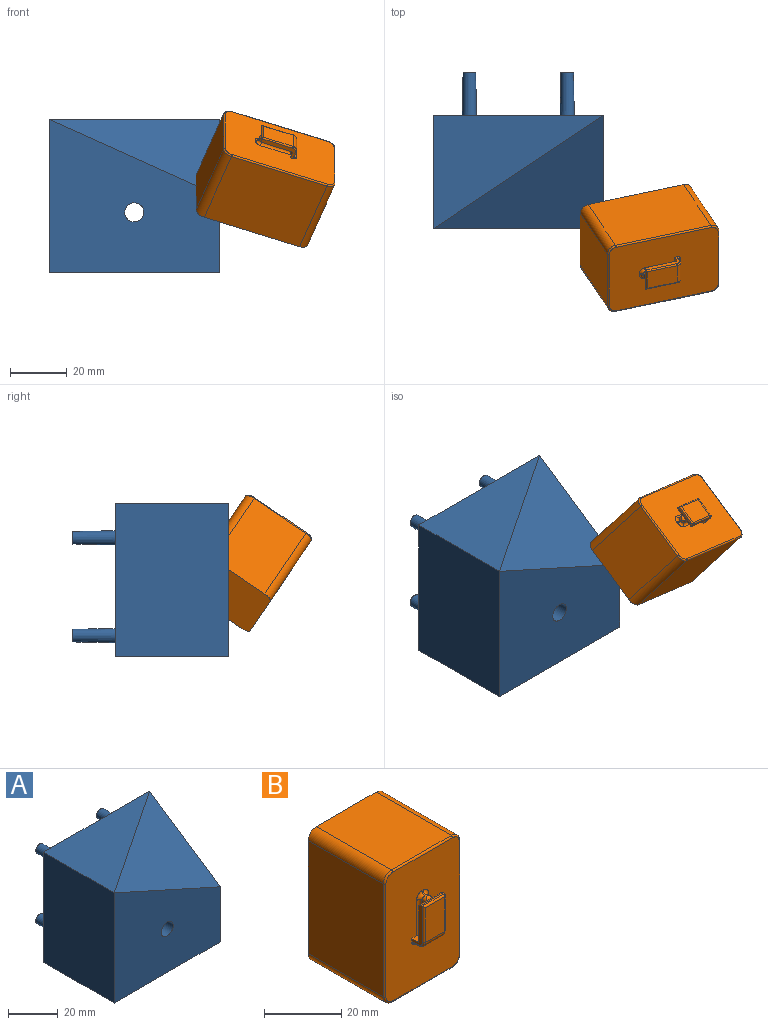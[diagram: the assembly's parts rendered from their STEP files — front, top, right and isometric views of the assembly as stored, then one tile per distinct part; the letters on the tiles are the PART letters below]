
ASSEMBLY  parts=2 mates=1
PART A: 16 faces, bbox 60x55x54 mm
  f0: plane 54x40mm, normal (1,0,0), area 1620mm2, adj f2,f4,f5,f15
  f1: plane 60x40mm, normal (0,0,1), area 1200mm2, adj f3,f5,f15
  f2: plane 60x54mm, normal (0,-1,0), area 2394.2mm2, adj f0,f3,f4,f14,f15
  f3: plane 54x40mm, normal (-1,0,0), area 2160mm2, adj f1,f2,f4,f5
  f4: plane 60x40mm, normal (0,0,-1), area 2400mm2, adj f0,f2,f3,f5
  f5: plane 60x54mm, normal (0,1,0), area 3125.7mm2, adj f0,f1,f3,f4,f6,f8,f10,f12
  f6: cone r=2.5mm half-angle=1deg, axis (0,-1,0), area 223.3mm2, adj f5,f7
  f7: plane 4.48x4.48mm, normal (0,1,0), area 15.7mm2, adj f6
  f8: cone r=2.5mm half-angle=1deg, axis (0,-1,0), area 223.3mm2, adj f5,f9
  f9: plane 4.48x4.48mm, normal (0,1,0), area 15.7mm2, adj f8
  f10: cone r=2.5mm half-angle=1deg, axis (0,-1,0), area 223.3mm2, adj f5,f11
  f11: plane 4.48x4.48mm, normal (0,1,0), area 15.7mm2, adj f10
  f12: cone r=2.5mm half-angle=1deg, axis (0,-1,0), area 223.3mm2, adj f5,f13
  f13: plane 4.48x4.48mm, normal (0,1,0), area 15.7mm2, adj f12
  f14: cylinder r=3.38mm len=40mm, axis (0,-1,0), area 848.2mm2, adj f2,f5
  f15: plane 60x40mm, normal (0.35,-0.52,0.78), area 1545.2mm2, adj f0,f1,f2
PART B: 49 faces, bbox 28.5x32.8x42.4 mm
  f0: plane 35.8x27.5mm, normal (1,0,0), area 984.5mm2, adj f1,f7,f46,f48
  f1: cylinder r=3mm len=27.5mm, axis (0,1,0), area 129.6mm2, adj f0,f2,f44,f48
  f2: plane 27.5x21.9mm, normal (0,0,1), area 602.2mm2, adj f1,f3,f42,f48
  f3: cylinder r=3mm len=27.5mm, axis (0,1,0), area 129.6mm2, adj f2,f4,f40,f48
  f4: plane 35.8x27.5mm, normal (-1,0,0), area 984.5mm2, adj f3,f5,f41,f48
  f5: cylinder r=3mm len=27.5mm, axis (0,1,0), area 129.6mm2, adj f4,f6,f43,f48
  f6: plane 27.5x21.9mm, normal (0,0,-1), area 602.2mm2, adj f5,f7,f45,f48
  f7: cylinder r=3mm len=27.5mm, axis (0,1,0), area 129.6mm2, adj f0,f6,f47,f48
  f8: plane 40.95x27.05mm, normal (0,-1,0), area 1016.5mm2, adj f9,f11,f12,f16,f18,f20,f22,f23
  f9: plane 13.42x4mm, normal (-1,0,0), area 21mm2, adj f8,f16,f25,f26,f29,f33,f34,f36
  f10: plane 7x1.5mm, normal (0,0,-1), area 10.5mm2, adj f28,f35,f36,f38
  f11: plane 13.42x4mm, normal (1,0,0), area 21mm2, adj f8,f12,f25,f26,f29,f30,f31,f38
  f12: plane 2.75x2.5mm, normal (0,0,1), area 6.7mm2, adj f8,f11,f13,f24,f25
  f13: plane 11.2x1.5mm, normal (1,0,0), area 16.8mm2, adj f12,f21,f24,f25
  f14: plane 0.5x0.5mm, normal (0,0,1), area 0.2mm2, adj f17,f19,f21,f22
  f15: plane 11.2x1.5mm, normal (-1,0,0), area 16.8mm2, adj f16,f17,f18,f25
  f16: plane 2.75x2.5mm, normal (0,0,1), area 6.7mm2, adj f8,f9,f15,f18,f25
  f17: cylinder r=1mm len=1.5mm, axis (0,-1,0), area 1.8mm2, adj f14,f15,f19,f20
  f18: cylinder r=1mm len=11.2mm, axis (0,0,-1), area 17.6mm2, adj f8,f15,f16,f20
  f19: cylinder r=1mm len=2.5mm, axis (1,0,0), area 2.8mm2, adj f14,f17,f21,f25
  f20: torus R=2mm, axis (0,-1,0), area 3.4mm2, adj f8,f17,f18,f22
  f21: cylinder r=1mm len=1.5mm, axis (0,1,0), area 1.8mm2, adj f13,f14,f19,f23
  f22: cylinder r=1mm len=1mm, axis (-1,0,0), area 0.8mm2, adj f8,f14,f20,f23
  f23: torus R=2mm, axis (0,-1,0), area 3.4mm2, adj f8,f21,f22,f24
  f24: cylinder r=1mm len=11.2mm, axis (0,0,1), area 17.6mm2, adj f8,f12,f13,f23
  f25: plane 11.24x8mm, normal (0,1,0), area 61.9mm2, adj f9,f11,f12,f13,f15,f16,f19,f29
  f26: plane 8x0.5mm, normal (0,0,1), area 4mm2, adj f9,f11,f29,f32
  f27: plane 11.04x7mm, normal (0,-1,0), area 77.3mm2, adj f28,f31,f32,f33
  f28: cylinder r=2mm len=7mm, axis (-1,0,0), area 22mm2, adj f10,f27,f30,f34
  f29: cylinder r=1mm len=8mm, axis (-1,0,0), area 12.6mm2, adj f9,f11,f25,f26
  f30: torus R=1.5mm, axis (-1,0,0), area 2.2mm2, adj f11,f28,f31,f38
  f31: cylinder r=0.5mm len=11.54mm, axis (0,0,-1), area 8.9mm2, adj f11,f27,f30,f32
  f32: cylinder r=0.5mm len=8mm, axis (1,0,0), area 5.9mm2, adj f26,f27,f31,f33
  f33: cylinder r=0.5mm len=11.54mm, axis (0,0,1), area 8.9mm2, adj f9,f27,f32,f34
  f34: torus R=1.5mm, axis (-1,0,0), area 2.2mm2, adj f9,f28,f33,f36
  f35: cylinder r=1mm len=7mm, axis (1,0,0), area 11mm2, adj f8,f10,f37,f39
  f36: cylinder r=0.5mm len=1.5mm, axis (0,1,0), area 1.2mm2, adj f9,f10,f34,f37
  f37: torus R=1.5mm, axis (1,0,0), area 1mm2, adj f8,f9,f35,f36
  f38: cylinder r=0.5mm len=1.5mm, axis (0,-1,0), area 1.2mm2, adj f10,f11,f30,f39
  f39: torus R=1.5mm, axis (1,0,0), area 1mm2, adj f8,f11,f35,f38
  f40: torus R=2.5mm, axis (0,-1,0), area 3.5mm2, adj f3,f8,f41,f42
  f41: cylinder r=0.5mm len=35.8mm, axis (0,0,1), area 28.1mm2, adj f4,f8,f40,f43
  f42: cylinder r=0.5mm len=21.9mm, axis (1,0,0), area 17.2mm2, adj f2,f8,f40,f44
  f43: torus R=2.5mm, axis (0,-1,0), area 3.5mm2, adj f5,f8,f41,f45
  f44: torus R=2.5mm, axis (0,-1,0), area 3.5mm2, adj f1,f8,f42,f46
  f45: cylinder r=0.5mm len=21.9mm, axis (-1,0,0), area 17.2mm2, adj f6,f8,f43,f47
  f46: cylinder r=0.5mm len=35.8mm, axis (0,0,-1), area 28.1mm2, adj f0,f8,f44,f47
  f47: torus R=2.5mm, axis (0,-1,0), area 3.5mm2, adj f7,f8,f45,f46
  f48: plane 41.8x27.9mm, normal (0,1,0), area 1158.5mm2, adj f0,f1,f2,f3,f4,f5,f6,f7
PLACE A t=(-7.34,-32.26,15.46)mm fixed
PLACE B rot(axis=(-0.29,-0.75,0.59),95.3deg) t=(42.77,-84.87,30.09)mm
MATE planar B.f48 <-> A.f15  axis (-0.35,0.52,-0.78) through (34.04,-71.77,10.67)mm
